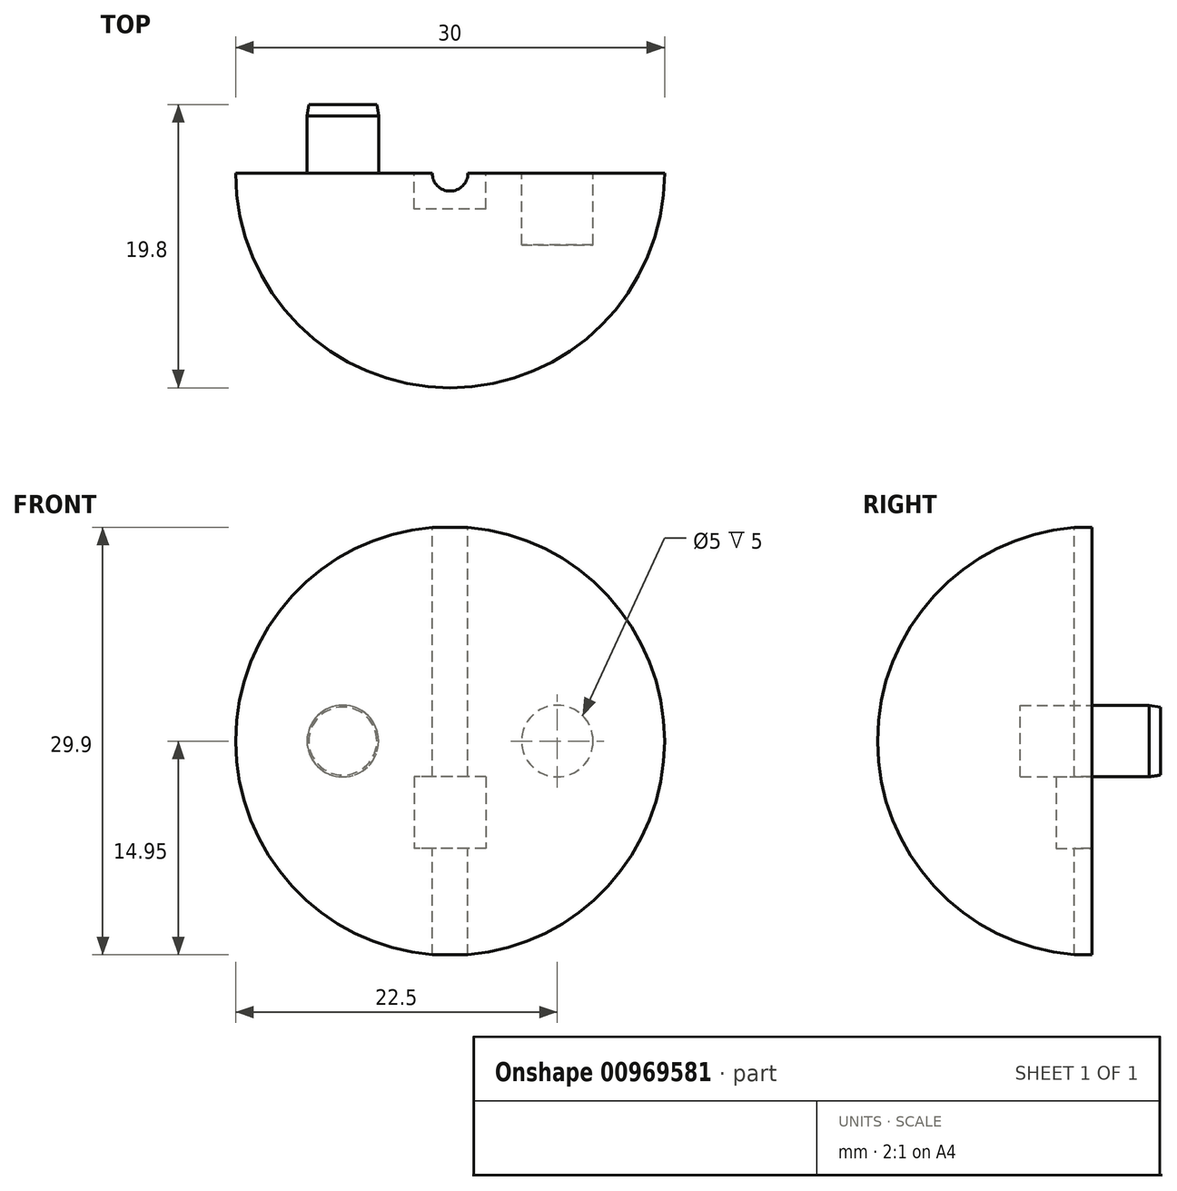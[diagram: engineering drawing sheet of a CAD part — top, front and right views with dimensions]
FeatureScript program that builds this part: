
annotation { "Feature Type Name" : "Feature", "Feature Type Description" : "" }
export const myFeature = defineFeature(function(context is Context, id is Id, definition is map)
    precondition{}
    {
        {
            var Q0;
            Q0=qCreatedBy(makeId("Front.planeOp"),FACE);
            var sketch = newSketch(context, id + "F0", { "sketchPlane" : qUnion([Q0])});
            skArc(sketch, "E0", {"start": v(-15, 0) * mm, "mid": v(0, 15) * mm, "end": v(15, 0) * mm});
            skLineSegment(sketch, "E1", {"start": v(-15, 0) * mm, "end": v(15, 0) * mm});
            skSolve(sketch);
        }
        {
            var Q0;
            Q0 = qSketchRegion(id + "F0", true);
            var Q1;
            Q1=sQuery(id+"F0.wireOp",EDGE,"E1");
            revolve(context, id + "F1", {"surfaceOperationType" : NewSurfaceOperationType.NEW, "entities" : qUnion([Q0]), "axis" : qUnion([Q1]), "revolveType" : RevolveType.ONE_DIRECTION, "angle" : 180 * degree});
        }
        {
            var Q0;
            Q0=qCreatedBy(makeId("Top.planeOp"),FACE);
            cPlane(context, id + "F2", {"entities" : qUnion([Q0]), "cplaneType" : CPlaneType.OFFSET, "offset" : 15 * mm, "width" : 150 * mm, "height" : 150 * mm});
        }
        {
            var Q0;
            Q0=qCreatedBy(id+"F2.planeOp",FACE);
            var sketch = newSketch(context, id + "F3", { "sketchPlane" : qUnion([Q0])});
            skArc(sketch, "E2", {"start": v(-1.25, 0) * mm, "mid": v(0, -1.25) * mm, "end": v(1.25, 0) * mm});
            skLineSegment(sketch, "E3", {"start": v(-1.25, 0) * mm, "end": v(1.25, 0) * mm});
            skSolve(sketch);
        }
        {
            var Q0;
            Q0=qCreatedBy(makeId("Front.planeOp"),FACE);
            var sketch = newSketch(context, id + "F4", { "sketchPlane" : qUnion([Q0])});
            skCircle(sketch, "E4", {"center": v(7.5, 0) * mm, "radius": 2.5 * mm});
            skSolve(sketch);
        }
        {
            var Q0;
            Q0 = qSketchRegion(id + "F4", true);
            extrude(context, id + "F5", {"entities" : qUnion([Q0]), "operationType" : NewBodyOperationType.REMOVE, "depth" : 5 * mm, "offsetDistance" : 25 * mm});
        }
        {
            var Q0;
            Q0=qCreatedBy(makeId("Front.planeOp"),FACE);
            var sketch = newSketch(context, id + "F6", { "sketchPlane" : qUnion([Q0])});
            skCircle(sketch, "E5", {"center": v(-7.5, 0) * mm, "radius": 2.5 * mm});
            skSolve(sketch);
        }
        {
            var Q0;
            Q0 = qSketchRegion(id + "F6", true);
            extrude(context, id + "F7", {"entities" : qUnion([Q0]), "operationType" : NewBodyOperationType.ADD, "oppositeDirection" : true, "depth" : 4 * mm, "offsetDistance" : 25 * mm});
        }
        {
            var Q0;
            Q0=qCreatedBy(makeId("Front.planeOp"),FACE);
            cPlane(context, id + "F8", {"entities" : qUnion([Q0]), "cplaneType" : CPlaneType.OFFSET, "offset" : 4.8 * mm, "oppositeDirection" : true, "width" : 150 * mm, "height" : 150 * mm});
        }
        {
            var Q0;
            Q0=qCreatedBy(id+"F8.planeOp",FACE);
            var sketch = newSketch(context, id + "F9", { "sketchPlane" : qUnion([Q0])});
            skCircle(sketch, "E6", {"center": v(-7.5, 0) * mm, "radius": 2.38 * mm});
            skSolve(sketch);
        }
        {
            var Q1;
            Q1=makeQuery(id+"F7.opExtrude","CAP_FACE",FACE,{"disambiguationData":[OSD([sQuery(id+"F6.wireOp",EDGE,"E5")])],"isStart":false});
            var Q2;
            Q2=makeQuery(id+"F9.imprint","IMPRINT",FACE,{"disambiguationData":[TD([[makeQuery(id+"F9.imprint","IMPRINT",EDGE,{"derivedFrom":sQuery(id+"F9.wireOp",EDGE,"E6")}),1.0]])]});
            loft(context, id + "F10", {"operationType" : NewBodyOperationType.ADD, "sheetProfilesArray" : [{ "sheetProfileEntities" : qUnion([Q1]) }, { "sheetProfileEntities" : qUnion([Q2]) }]});
        }
        {
            var Q0;
            Q0 = qSketchRegion(id + "F3", true);
            extrude(context, id + "F11", {"entities" : qUnion([Q0]), "operationType" : NewBodyOperationType.REMOVE, "oppositeDirection" : true, "depth" : 30 * mm, "offsetDistance" : 25 * mm});
        }
        {
            var Q0;
            Q0=qCreatedBy(makeId("Front.planeOp"),FACE);
            var sketch = newSketch(context, id + "F12", { "sketchPlane" : qUnion([Q0])});
            skLineSegment(sketch, "E7", {"start": v(0, 0) * mm, "end": v(0, -5) * mm});
            skLineSegment(sketch, "E8.bottom", {"start": v(2.5, -2.5) * mm, "end": v(-2.5, -2.5) * mm});
            skLineSegment(sketch, "E8.top", {"start": v(2.5, -7.5) * mm, "end": v(-2.5, -7.5) * mm});
            skLineSegment(sketch, "E8.left", {"start": v(2.5, -2.5) * mm, "end": v(2.5, -7.5) * mm});
            skLineSegment(sketch, "E8.right", {"start": v(-2.5, -2.5) * mm, "end": v(-2.5, -7.5) * mm});
            skPoint(sketch, "E8.middle", {"position": v(0, -5) * mm});
            skSolve(sketch);
        }
        {
            var Q0;
            Q0 = qSketchRegion(id + "F12", true);
            extrude(context, id + "F13", {"entities" : qUnion([Q0]), "operationType" : NewBodyOperationType.REMOVE, "depth" : 2.5 * mm, "offsetDistance" : 25 * mm});
        }
    });
